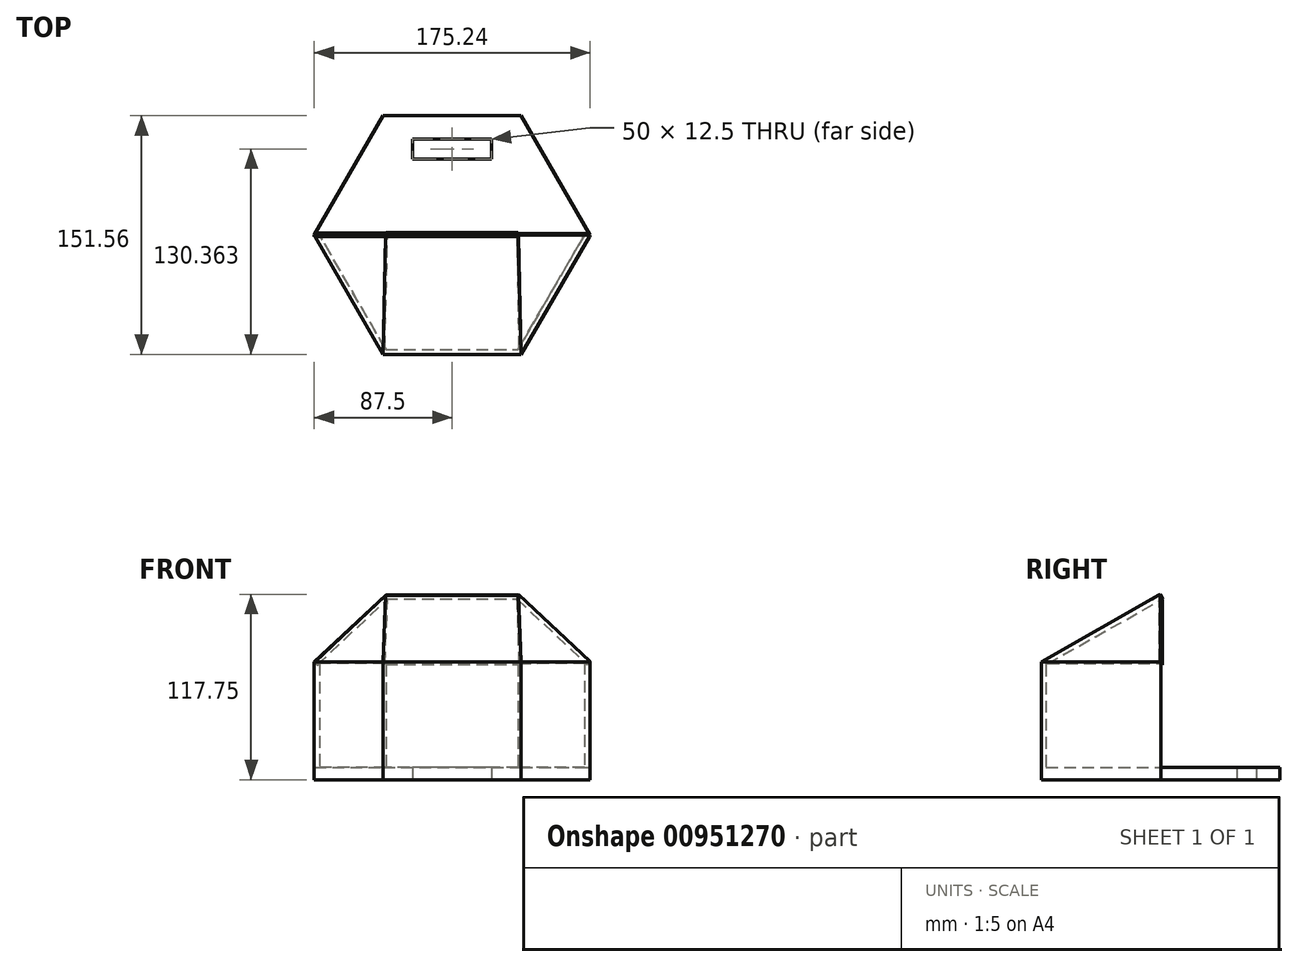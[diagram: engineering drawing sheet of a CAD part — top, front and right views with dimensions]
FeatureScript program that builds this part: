
annotation { "Feature Type Name" : "Feature", "Feature Type Description" : "" }
export const myFeature = defineFeature(function(context is Context, id is Id, definition is map)
    precondition{}
    {
        {
            var Q0;
            Q0=qCreatedBy(makeId("Top.planeOp"),FACE);
            var sketch = newSketch(context, id + "F0", { "sketchPlane" : qUnion([Q0])});
            skCircle(sketch, "E0.cCircle", {"center": v(0, 0) * mm, "radius": 75.78 * mm, "construction": true});
            skLineSegment(sketch, "E0.0", {"start": v(-43.75, 75.78) * mm, "end": v(43.75, 75.78) * mm});
            skLineSegment(sketch, "E0.1", {"start": v(43.75, 75.78) * mm, "end": v(87.5, 0) * mm});
            skLineSegment(sketch, "E0.2", {"start": v(87.5, 0) * mm, "end": v(43.75, -75.78) * mm});
            skLineSegment(sketch, "E0.3", {"start": v(43.75, -75.78) * mm, "end": v(-43.75, -75.78) * mm});
            skLineSegment(sketch, "E0.4", {"start": v(-43.75, -75.78) * mm, "end": v(-87.5, 0) * mm});
            skLineSegment(sketch, "E0.5", {"start": v(-87.5, 0) * mm, "end": v(-43.75, 75.78) * mm});
            skPoint(sketch, "E0.0.midPoint", {"position": v(0, 75.78) * mm});
            skLineSegment(sketch, "E1.0", {"start": v(-84.04, 0) * mm, "end": v(-42.02, 72.78) * mm});
            skLineSegment(sketch, "E1.1", {"start": v(42.02, 72.78) * mm, "end": v(84.04, 0) * mm});
            skLineSegment(sketch, "E1.2", {"start": v(84.04, 0) * mm, "end": v(42.02, -72.78) * mm});
            skLineSegment(sketch, "E1.3", {"start": v(-42.02, 72.78) * mm, "end": v(42.02, 72.78) * mm});
            skLineSegment(sketch, "E1.4", {"start": v(42.02, -72.78) * mm, "end": v(-42.02, -72.78) * mm});
            skLineSegment(sketch, "E1.5", {"start": v(-42.02, -72.78) * mm, "end": v(-84.04, 0) * mm});
            skLineSegment(sketch, "E2", {"start": v(-87.5, 0) * mm, "end": v(-84.04, 0) * mm});
            skLineSegment(sketch, "E3", {"start": v(84.04, 0) * mm, "end": v(87.5, 0) * mm});
            skLineSegment(sketch, "E4", {"start": v(0, 0) * mm, "end": v(0, 72.78) * mm, "construction": true});
            skLineSegment(sketch, "E5", {"start": v(0, 0) * mm, "end": v(42.02, 72.78) * mm, "construction": true});
            skLineSegment(sketch, "E6", {"start": v(0, 0) * mm, "end": v(-42.02, 72.78) * mm, "construction": true});
            skLineSegment(sketch, "E7", {"start": v(0, 36.39) * mm, "end": v(0, 72.78) * mm, "construction": true});
            skLineSegment(sketch, "E8.bottom", {"start": v(25, 48.33) * mm, "end": v(-25, 48.33) * mm});
            skLineSegment(sketch, "E8.top", {"start": v(25, 60.83) * mm, "end": v(-25, 60.83) * mm});
            skLineSegment(sketch, "E8.left", {"start": v(25, 48.33) * mm, "end": v(25, 60.83) * mm});
            skLineSegment(sketch, "E8.right", {"start": v(-25, 48.33) * mm, "end": v(-25, 60.83) * mm});
            skPoint(sketch, "E8.middle", {"position": v(0, 54.58) * mm});
            skSolve(sketch);
        }
        {
            var Q0;
            Q0=makeQuery(id+"F0.imprint","IMPRINT",FACE,{"disambiguationData":[TD([[makeQuery(id+"F0.imprint","IMPRINT",EDGE,{"derivedFrom":sQuery(id+"F0.wireOp",EDGE,"E1.0")}),-1.0]])]});
            extrude(context, id + "F1", {"entities" : qUnion([Q0]), "depth" : 8 * mm, "offsetDistance" : 25 * mm});
        }
        {
            var Q0;
            Q0=makeQuery(id+"F0.imprint","IMPRINT",FACE,{"disambiguationData":[TD([[makeQuery(id+"F0.imprint","IMPRINT",EDGE,{"derivedFrom":sQuery(id+"F0.wireOp",EDGE,"E0.2")}),-1.0]])]});
            extrude(context, id + "F2", {"entities" : qUnion([Q0]), "operationType" : NewBodyOperationType.ADD, "depth" : 75 * mm, "offsetDistance" : 25 * mm});
        }
        {
            var Q0;
            Q0=qCreatedBy(makeId("Front.planeOp"),FACE);
            var sketch = newSketch(context, id + "F3", { "sketchPlane" : qUnion([Q0])});
            skLineSegment(sketch, "E9", {"start": v(0, 0) * mm, "end": v(0, 144.27) * mm, "construction": true});
            skLineSegment(sketch, "E10", {"start": v(0, 144.27) * mm, "end": v(-94, 144.27) * mm, "construction": true});
            skLineSegment(sketch, "E11", {"start": v(0, 144.27) * mm, "end": v(81.74, 144.27) * mm});
            skLineSegment(sketch, "E12", {"start": v(0, 0) * mm, "end": v(0, 75) * mm, "construction": true});
            skLineSegment(sketch, "E13", {"start": v(0, 75) * mm, "end": v(0, 114.5) * mm, "construction": true});
            skLineSegment(sketch, "E14", {"start": v(0, 75) * mm, "end": v(-87.5, 75) * mm, "construction": true});
            skLineSegment(sketch, "E15", {"start": v(0, 114.5) * mm, "end": v(42.02, 114.5) * mm, "construction": true});
            skLineSegment(sketch, "E16", {"start": v(0, 114.5) * mm, "end": v(-42.02, 114.5) * mm});
            skLineSegment(sketch, "E17", {"start": v(0, 75) * mm, "end": v(-84.04, 75) * mm, "construction": true});
            skLineSegment(sketch, "E18", {"start": v(-42.02, 114.5) * mm, "end": v(-84.04, 75) * mm});
            skLineSegment(sketch, "E19", {"start": v(-42.02, 114.5) * mm, "end": v(-42.02, 117.5) * mm, "construction": true});
            skLineSegment(sketch, "E20", {"start": v(-42.02, 117.5) * mm, "end": v(-87.5, 75) * mm});
            skLineSegment(sketch, "E21", {"start": v(-42.02, 117.5) * mm, "end": v(0, 117.5) * mm});
            skLineSegment(sketch, "E22.MirrorCS", {"start": v(42.02, 117.5) * mm, "end": v(87.5, 75) * mm});
            skLineSegment(sketch, "E23.MirrorCS", {"start": v(42.02, 114.5) * mm, "end": v(84.04, 75) * mm});
            skLineSegment(sketch, "E24.MirrorCS", {"start": v(42.02, 117.5) * mm, "end": v(0, 117.5) * mm});
            skLineSegment(sketch, "E25.MirrorCS", {"start": v(0, 114.5) * mm, "end": v(42.02, 114.5) * mm});
            skLineSegment(sketch, "E26", {"start": v(87.5, 75) * mm, "end": v(84.04, 75) * mm});
            skLineSegment(sketch, "E27", {"start": v(-84.04, 75) * mm, "end": v(-87.5, 75) * mm});
            skSolve(sketch);
        }
        {
            var Q0;
            Q0=makeQuery(id+"F0.imprint","IMPRINT",FACE,{"disambiguationData":[TD([[makeQuery(id+"F0.imprint","IMPRINT",EDGE,{"derivedFrom":sQuery(id+"F0.wireOp",EDGE,"E0.0")}),-1.0]])]});
            extrude(context, id + "F4", {"entities" : qUnion([Q0]), "operationType" : NewBodyOperationType.ADD, "oppositeDirection" : true, "depth" : -8 * mm, "offsetDistance" : 25 * mm});
        }
        {
            var Q0;
            Q0=makeQuery(id+"F2.opExtrude","CAP_EDGE",EDGE,{"disambiguationData":[OSD([sQuery(id+"F0.wireOp",EDGE,"E0.3")])],"isStart":false});
            var Q1;
            Q1=sQuery(id+"F3.wireOp",VERTEX,"E21.end");
            cPlane(context, id + "F5", {"entities" : qUnion([Q0, Q1]), "cplaneType" : CPlaneType.LINE_ANGLE, "offset" : 25 * mm, "angle" : 0 * degree, "width" : 150 * mm, "height" : 150 * mm});
        }
        {
            var Q0;
            Q0=qCreatedBy(id+"F5.planeOp",FACE);
            var sketch = newSketch(context, id + "F6", { "sketchPlane" : qUnion([Q0])});
            skLineSegment(sketch, "E28", {"start": v(0, 29.4) * mm, "end": v(43.75, 29.4) * mm});
            skLineSegment(sketch, "E29", {"start": v(0, 29.4) * mm, "end": v(-43.75, 29.4) * mm});
            skLineSegment(sketch, "E30", {"start": v(-43.75, 29.4) * mm, "end": v(-42.02, -57.48) * mm});
            skLineSegment(sketch, "E31", {"start": v(43.75, 29.4) * mm, "end": v(42.02, -57.48) * mm});
            skLineSegment(sketch, "E32", {"start": v(-42.02, -57.48) * mm, "end": v(42.02, -57.48) * mm});
            skSolve(sketch);
        }
        {
            var Q0;
            Q0=makeQuery(id+"F6.imprint","IMPRINT",FACE,{"disambiguationData":[TD([[makeQuery(id+"F6.imprint","IMPRINT",EDGE,{"derivedFrom":sQuery(id+"F6.wireOp",EDGE,"E28")}),-1.0]])]});
            extrude(context, id + "F7", {"entities" : qUnion([Q0]), "operationType" : NewBodyOperationType.ADD, "depth" : 3 * mm, "offsetDistance" : 25 * mm});
        }
        {
            var Q0;
            Q0=makeQuery(id+"F3.imprint","IMPRINT",FACE,{"disambiguationData":[TD([[makeQuery(id+"F3.imprint","IMPRINT",EDGE,{"derivedFrom":sQuery(id+"F3.wireOp",EDGE,"E16")}),-1.0]])]});
            extrude(context, id + "F8", {"entities" : qUnion([Q0]), "operationType" : NewBodyOperationType.ADD, "depth" : 1 * mm, "offsetDistance" : 25 * mm});
        }
        {
            var Q0;
            Q0=makeQuery(id+"F8.opExtrude","CAP_EDGE",EDGE,{"disambiguationData":[OSD([sQuery(id+"F3.wireOp",EDGE,"E20")])],"isStart":true});
            var Q1;
            Q1=makeQuery(id+"F7.boolean.opBoolean","MERGE",VERTEX,{"derivedFrom":[makeQuery(id+"F2.opExtrude","CAP_VERTEX",VERTEX,{"disambiguationData":[OSD([sQuery(id+"F0.wireOp",EDGE,"E0.3"),sQuery(id+"F0.wireOp",EDGE,"E0.4")])],"isStart":false}),makeQuery(id+"F7.opExtrude","CAP_VERTEX",VERTEX,{"disambiguationData":[OSD([sQuery(id+"F6.wireOp",EDGE,"E29"),sQuery(id+"F6.wireOp",EDGE,"E30")])],"isStart":true})]});
            cPlane(context, id + "F9", {"entities" : qUnion([Q0, Q1]), "cplaneType" : CPlaneType.LINE_ANGLE, "offset" : 25 * mm, "angle" : 0 * degree, "width" : 150 * mm, "height" : 150 * mm});
        }
        {
            var Q0;
            Q0=qCreatedBy(id+"F9.planeOp",FACE);
            var sketch = newSketch(context, id + "F10", { "sketchPlane" : qUnion([Q0])});
            skLineSegment(sketch, "E33", {"start": v(-25.66, 35.61) * mm, "end": v(30.99, -31.08) * mm});
            skLineSegment(sketch, "E34", {"start": v(-25.66, 35.61) * mm, "end": v(33.23, 55.79) * mm});
            skLineSegment(sketch, "E35", {"start": v(33.23, 55.79) * mm, "end": v(30.99, -31.08) * mm});
            skSolve(sketch);
        }
        {
            var Q0;
            Q0 = qSketchRegion(id + "F10", true);
            extrude(context, id + "F11", {"entities" : qUnion([Q0]), "operationType" : NewBodyOperationType.ADD, "depth" : -3 * mm, "offsetDistance" : 25 * mm});
        }
        {
            var Q0;
            Q0=makeQuery(id+"F8.opExtrude","CAP_EDGE",EDGE,{"disambiguationData":[OSD([sQuery(id+"F3.wireOp",EDGE,"E22.MirrorCS")])],"isStart":false});
            var Q1;
            Q1=makeQuery(id+"F7.boolean.opBoolean","MERGE",VERTEX,{"derivedFrom":[makeQuery(id+"F2.opExtrude","CAP_VERTEX",VERTEX,{"disambiguationData":[OSD([sQuery(id+"F0.wireOp",EDGE,"E0.2"),sQuery(id+"F0.wireOp",EDGE,"E0.3")])],"isStart":false}),makeQuery(id+"F7.opExtrude","CAP_VERTEX",VERTEX,{"disambiguationData":[OSD([sQuery(id+"F6.wireOp",EDGE,"E28"),sQuery(id+"F6.wireOp",EDGE,"E31")])],"isStart":true})]});
            cPlane(context, id + "F12", {"entities" : qUnion([Q0, Q1]), "cplaneType" : CPlaneType.LINE_ANGLE, "offset" : 25 * mm, "angle" : 0 * degree, "width" : 150 * mm, "height" : 150 * mm});
        }
        {
            var Q0;
            Q0=qCreatedBy(id+"F12.planeOp",FACE);
            var sketch = newSketch(context, id + "F13", { "sketchPlane" : qUnion([Q0])});
            skLineSegment(sketch, "E36", {"start": v(-32.88, -56.36) * mm, "end": v(25.94, -35.98) * mm});
            skLineSegment(sketch, "E37", {"start": v(25.94, -35.98) * mm, "end": v(-30.94, 30.51) * mm});
            skLineSegment(sketch, "E38", {"start": v(-30.94, 30.51) * mm, "end": v(-32.88, -56.36) * mm});
            skSolve(sketch);
        }
        {
            var Q0;
            Q0 = qSketchRegion(id + "F13", true);
            extrude(context, id + "F14", {"entities" : qUnion([Q0]), "operationType" : NewBodyOperationType.ADD, "depth" : 3 * mm, "offsetDistance" : 25 * mm});
        }
    });
